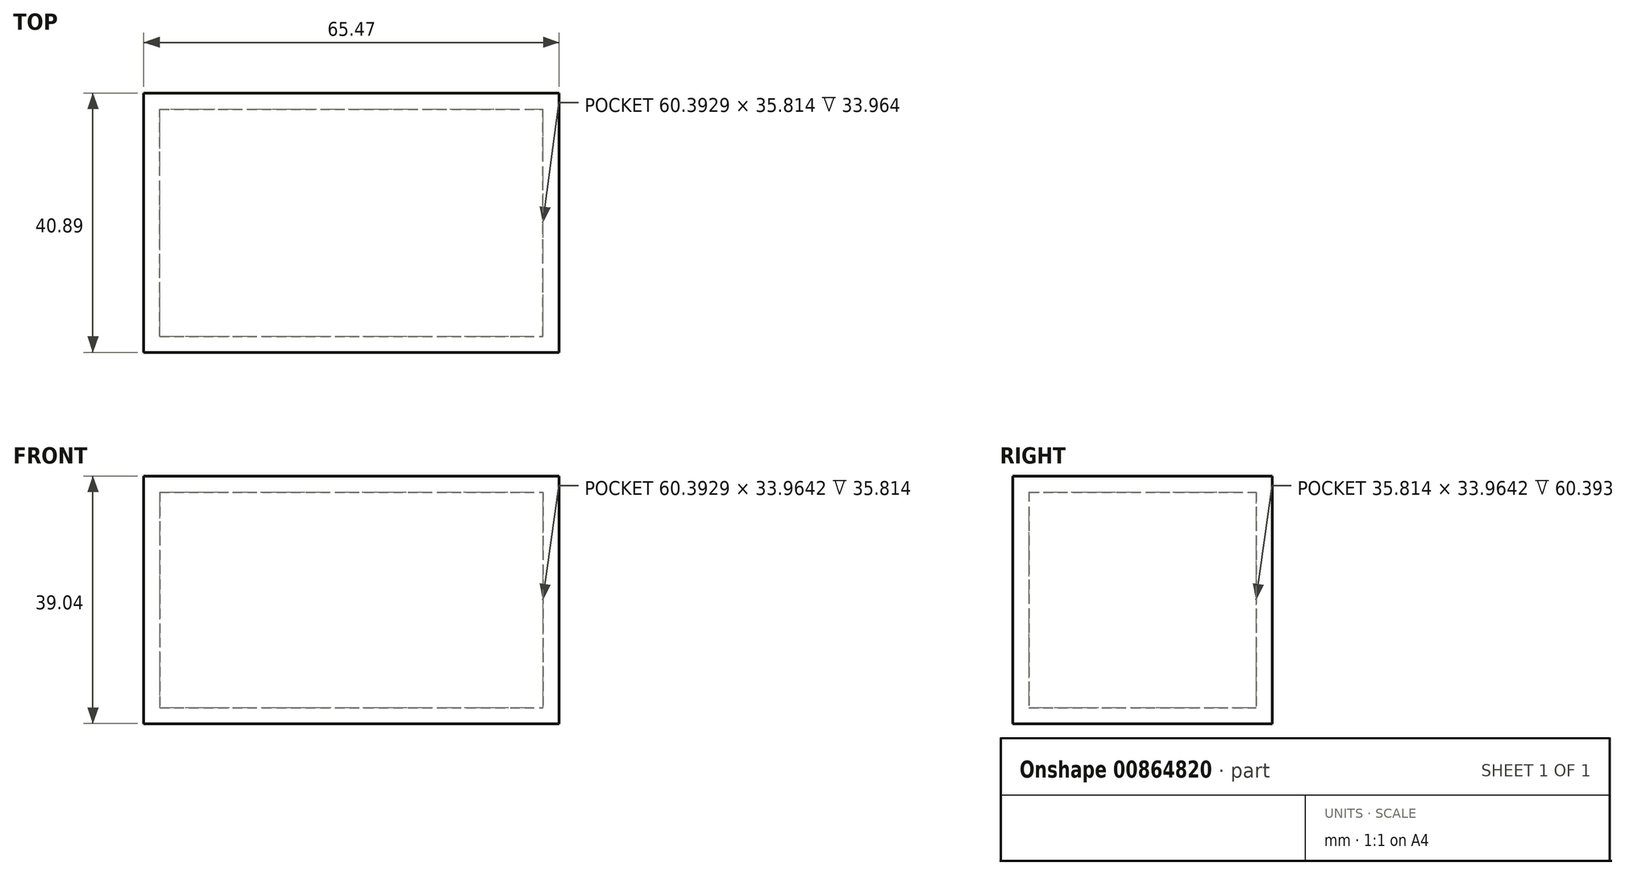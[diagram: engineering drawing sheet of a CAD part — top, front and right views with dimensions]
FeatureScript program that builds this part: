
annotation { "Feature Type Name" : "Feature", "Feature Type Description" : "" }
export const myFeature = defineFeature(function(context is Context, id is Id, definition is map)
    precondition{}
    {
        {
            var Q0;
            Q0=qCreatedBy(makeId("Front.planeOp"),FACE);
            var sketch = newSketch(context, id + "F0", { "sketchPlane" : qUnion([Q0])});
            skLineSegment(sketch, "E0.bottom", {"start": v(-70.27, 46.13) * mm, "end": v(-9.88, 46.13) * mm});
            skLineSegment(sketch, "E0.top", {"start": v(-70.27, 12.17) * mm, "end": v(-9.88, 12.17) * mm});
            skLineSegment(sketch, "E0.left", {"start": v(-70.27, 46.13) * mm, "end": v(-70.27, 12.17) * mm});
            skLineSegment(sketch, "E0.right", {"start": v(-9.88, 46.13) * mm, "end": v(-9.88, 12.17) * mm});
            skSolve(sketch);
        }
        {
            var Q0;
            Q0=makeQuery(id+"F0.imprint","IMPRINT",FACE,{"disambiguationData":[TD([[makeQuery(id+"F0.imprint","IMPRINT",EDGE,{"derivedFrom":sQuery(id+"F0.wireOp",EDGE,"E0.bottom")}),-1.0]])]});
            extrude(context, id + "F1", {"entities" : qUnion([Q0]), "depth" : 35.81 * mm, "offsetDistance" : 25.4 * mm});
        }
        {
            var Q0;
            Q0=makeQuery(id+"F1.opExtrude","CAP_FACE",FACE,{"disambiguationData":[OSD([sQuery(id+"F0.wireOp",EDGE,"E0.bottom"),sQuery(id+"F0.wireOp",EDGE,"E0.top"),sQuery(id+"F0.wireOp",EDGE,"E0.left"),sQuery(id+"F0.wireOp",EDGE,"E0.right")])],"isStart":false});
            var Q1;
            Q1=makeQuery(id+"F1.opExtrude","SWEPT_BODY",BODY,{"disambiguationData":[OSD([sQuery(id+"F0.wireOp",EDGE,"E0.bottom"),sQuery(id+"F0.wireOp",EDGE,"E0.top"),sQuery(id+"F0.wireOp",EDGE,"E0.left"),sQuery(id+"F0.wireOp",EDGE,"E0.right")])]});
            shell(context, id + "F2", {"isHollow" : true, "entities" : qUnion([Q0]), "parts" : qUnion([Q1]), "thickness" : 2.54 * mm, "oppositeDirection" : true});
        }
    });
